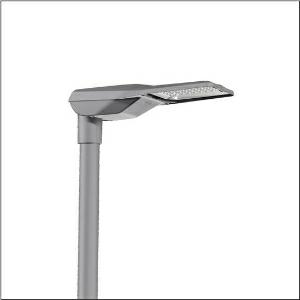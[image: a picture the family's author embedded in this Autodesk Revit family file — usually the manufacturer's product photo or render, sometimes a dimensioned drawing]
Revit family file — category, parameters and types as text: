
# Revit family: streetlight_sl_21_iq_mini___stw1_0a_5xe2e41d08hb_667c
name_source: partatom
category: Lighting Fixtures
units: mm (PartAtom-declared; Revit-internal decimal feet)

## family parameters
Cut with Voids When Loaded = No
Host = Face
Light Source = No
Part Type = Normal
Room Calculation Point = No
Round Connector Dimension = Use Diameter
Shared = No

## types (1)
- --- (1 x LED, 9860 lm, 70.9 W, 4000K)
    Apparent Load = 71 VA
    CIE Flux Codes = 38 75 98 100 100
    Color Rendering = 70
    Color Temperature = 4000K
    Default Elevation = 1800 mm
    Description = Streetlight SL 21 mini, mast luminaire, primary light control with lens, of PMMA, primary optical cover: cover, of toughened safety glass, transparent, light distribution: STW1.0a, light emission: direct distribution, primary light characteristic: asymmetric, installation type: post-top, side-entry, LED, High Power LED, rated luminous flux: 9.860lm, luminous efficacy: 139lm/W, light colour: 740, colour temperature: 4000K, control gear: ECG iQ, control: Auto-Match, Temp-Guard, Lumen-Switch, Night-Set, Smart-Wire, Light-Fading, Desk-Remote (wireless, voltage-free reading and setting of iQ features in the workshop via application-optimized NFC function/RFID function), optimised constant luminous flux control (CLO 2.0), mains connection: 220..240V, AC, 50/60Hz, start of lifetime: 71W, end of lifetime: 75W, reduction: 31W, luminaire housing, of diecast aluminium, powder-coated, Siteco® metallic grey (DB 702S), corrosivity category C5 according to DIN EN ISO 12944, length: 628mm, width: 235mm, height: 110mm, spigot size: 60/76mm (post-top) and 42/60/76mm (side-entry), mast flange for spigot size: 42mm: 5XC10008XM4, 60mm: 5XC10008XM2, 76/60mm: 5XC10108XM1, protection rating (complete): IP66, insulation class (complete): insulation class II (safety insulation), certification: CE, ENEC, VDE, impact resistance: IK09, permissible operating ambient temperature for outdoor applications: -40..+50°C, standard-compliant lighting for roads and squares, packaging unit: 1 piece

Light Distribution: STW1.0a
    Height = 110 mm
    Lamp = 1 x LED
    Lamp Light Flux = 9860 lm
    Lamp Power = 70.9 W
    Lamp count = 1
    Length = 625 mm
    Luminous efficacy = 139 lm/W
    Manufacturer = Siteco
    ModVariant = No
    Model = 5XE2E41D08HB
    Number of Poles = 1
    OnlyDefault = Yes
    Power Factor = 1
    Product Name = Streetlight SL 21 iQ mini | STW1.0a
    Product group = mast luminaire | pylon top
    ProductGroupID = 6100
    Protection Class = Protection class II
    Protection Degree = IP 66
    RLX_Detail_Level = 1
    RlxData = <blob elided: 92049 chars, md5=21729e38>
    Socket = socket
    Standby Power = 0 W
    System Light Flux = 9860 lm
    System Power = 71 W
    Type Comments = factory setting: luminous flux: 100 % | dim-lin: 254 | 711 mA
    Type Image = l_1003519.jpg
    URL = http://relux.com
    VarID = @adj_069037
    Voltage = 0 V
    Weight = 0.00 kg
    Width = 234 mm

## geometry (parser evidence)
native form markers: Blend x4, Sweep x11
no freeform markers — native parametric forms only
